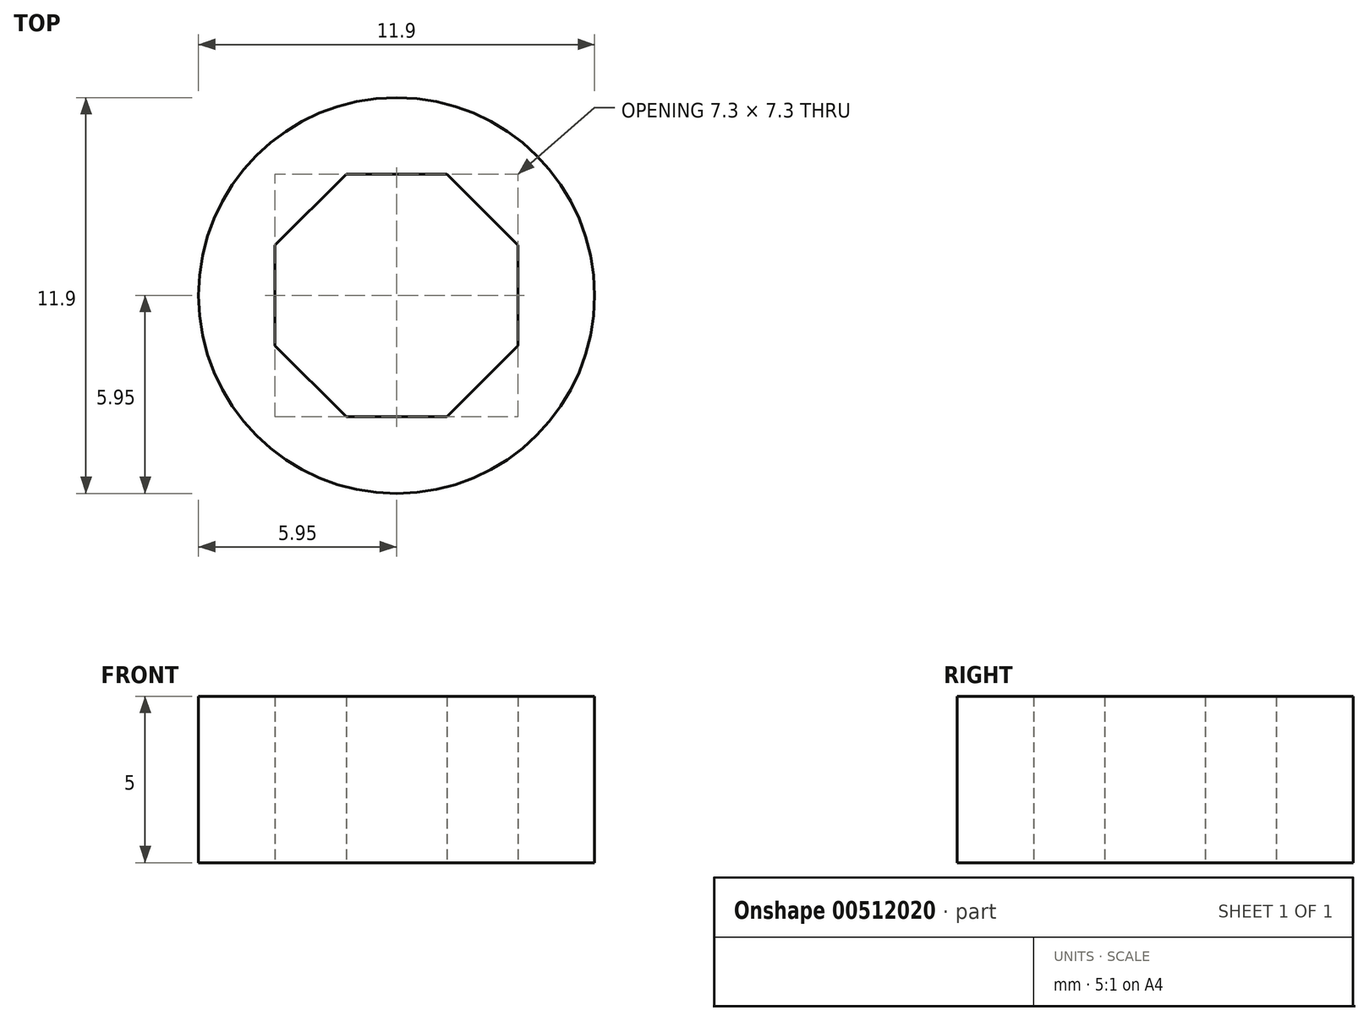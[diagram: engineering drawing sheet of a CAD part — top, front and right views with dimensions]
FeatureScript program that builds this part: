
annotation { "Feature Type Name" : "Feature", "Feature Type Description" : "" }
export const myFeature = defineFeature(function(context is Context, id is Id, definition is map)
    precondition{}
    {
        {
            var Q0;
            Q0=qCreatedBy(makeId("Top.planeOp"),FACE);
            var sketch = newSketch(context, id + "F0", { "sketchPlane" : qUnion([Q0])});
            skCircle(sketch, "E0.cCircle", {"center": v(0, 0) * mm, "radius": 3.65 * mm, "construction": true});
            skLineSegment(sketch, "E0.0", {"start": v(3.65, 1.51) * mm, "end": v(3.65, -1.51) * mm});
            skLineSegment(sketch, "E0.1", {"start": v(3.65, -1.51) * mm, "end": v(1.51, -3.65) * mm});
            skLineSegment(sketch, "E0.2", {"start": v(1.51, -3.65) * mm, "end": v(-1.51, -3.65) * mm});
            skLineSegment(sketch, "E0.3", {"start": v(-1.51, -3.65) * mm, "end": v(-3.65, -1.51) * mm});
            skLineSegment(sketch, "E0.4", {"start": v(-3.65, -1.51) * mm, "end": v(-3.65, 1.51) * mm});
            skLineSegment(sketch, "E0.5", {"start": v(-3.65, 1.51) * mm, "end": v(-1.51, 3.65) * mm});
            skLineSegment(sketch, "E0.6", {"start": v(-1.51, 3.65) * mm, "end": v(1.51, 3.65) * mm});
            skLineSegment(sketch, "E0.7", {"start": v(1.51, 3.65) * mm, "end": v(3.65, 1.51) * mm});
            skPoint(sketch, "E0.0.midPoint", {"position": v(3.65, 0) * mm});
            skCircle(sketch, "E1", {"center": v(0, 0) * mm, "radius": 5.95 * mm});
            skSolve(sketch);
        }
        {
            var Q0;
            Q0 = qSketchRegion(id + "F0", true);
            extrude(context, id + "F1", {"entities" : qUnion([Q0]), "depth" : 5 * mm, "offsetDistance" : 25 * mm, "symmetric" : true});
        }
    });
